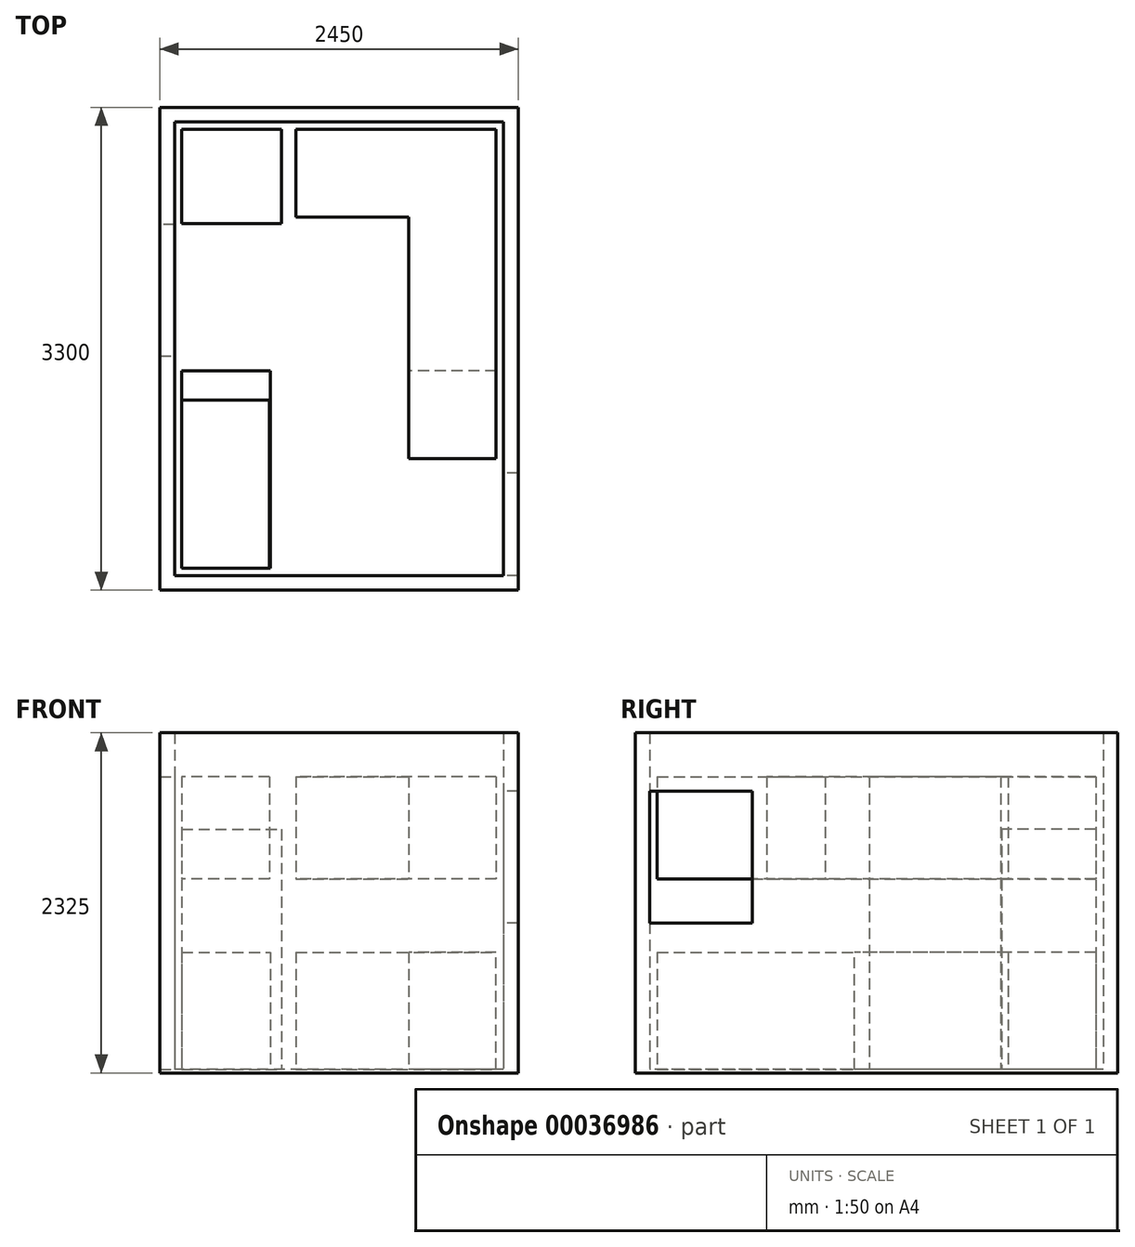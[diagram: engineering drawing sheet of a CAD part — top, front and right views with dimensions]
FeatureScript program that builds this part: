
annotation { "Feature Type Name" : "Feature", "Feature Type Description" : "" }
export const myFeature = defineFeature(function(context is Context, id is Id, definition is map)
    precondition{}
    {
        {
            var Q0;
            Q0=qCreatedBy(makeId("Top.planeOp"),FACE);
            var sketch = newSketch(context, id + "F0", { "sketchPlane" : qUnion([Q0])});
            skLineSegment(sketch, "E0.rect.bottom", {"start": v(1125, 1550) * mm, "end": v(-1125, 1550) * mm});
            skLineSegment(sketch, "E0.rect.top", {"start": v(1125, -1550) * mm, "end": v(-1125, -1550) * mm});
            skLineSegment(sketch, "E0.rect.left", {"start": v(1125, 1550) * mm, "end": v(1125, -1550) * mm});
            skLineSegment(sketch, "E0.rect.right", {"start": v(-1125, 1550) * mm, "end": v(-1125, -1550) * mm});
            skPoint(sketch, "E0.rect.middle", {"position": v(0, 0) * mm});
            skLineSegment(sketch, "E1.0", {"start": v(1225, 1650) * mm, "end": v(-1225, 1650) * mm});
            skLineSegment(sketch, "E1.1", {"start": v(1225, 1650) * mm, "end": v(1225, -1650) * mm});
            skLineSegment(sketch, "E1.2", {"start": v(1225, -1650) * mm, "end": v(-1225, -1650) * mm});
            skLineSegment(sketch, "E1.3", {"start": v(-1225, 1650) * mm, "end": v(-1225, -1650) * mm});
            skLineSegment(sketch, "E2", {"start": v(-1125, 850) * mm, "end": v(-1225, 850) * mm});
            skLineSegment(sketch, "E3", {"start": v(-1225, -50) * mm, "end": v(-1125, -50) * mm});
            skSolve(sketch);
        }
        {
            var Q0;
            {var subQ3=sQuery(id+"F0.wireOp",EDGE,"E0.rect.bottom");Q0=makeQuery(id+"F0.imprint","IMPRINT",FACE,{"disambiguationData":[TD([[makeQuery(id+"F0.imprint","IMPRINT",EDGE,{"derivedFrom":subQ3}),-1.0]])]});}
            extrude(context, id + "F1", {"entities" : qUnion([Q0]), "depth" : 2300 * mm});
        }
        {
            var Q0;
            Q0=makeQuery(id+"F1.opExtrude","SWEPT_FACE",FACE,{"disambiguationData":[OSD([sQuery(id+"F0.wireOp",EDGE,"E0.rect.left")])]});
            var sketch = newSketch(context, id + "F2", { "sketchPlane" : qUnion([Q0])});
            skLineSegment(sketch, "E4.bottom", {"start": v(1550, 1900) * mm, "end": v(850, 1900) * mm});
            skLineSegment(sketch, "E4.top", {"start": v(1550, 1000) * mm, "end": v(850, 1000) * mm});
            skLineSegment(sketch, "E4.left", {"start": v(1550, 1900) * mm, "end": v(1550, 1000) * mm});
            skLineSegment(sketch, "E4.right", {"start": v(850, 1900) * mm, "end": v(850, 1000) * mm});
            skSolve(sketch);
        }
        {
            var Q0;
            Q0 = qSketchRegion(id + "F2", true);
            extrude(context, id + "F3", {"entities" : qUnion([Q0]), "operationType" : NewBodyOperationType.REMOVE, "oppositeDirection" : true, "depth" : 512.68 * mm});
        }
        {
            var Q0;
            Q0=makeQuery(id+"F1.opExtrude","CAP_FACE",FACE,{"disambiguationData":[OSD([sQuery(id+"F0.wireOp",EDGE,"E0.rect.bottom"),sQuery(id+"F0.wireOp",EDGE,"E0.rect.top"),sQuery(id+"F0.wireOp",EDGE,"E0.rect.left"),sQuery(id+"F0.wireOp",EDGE,"E0.rect.right"),sQuery(id+"F0.wireOp",EDGE,"E1.0"),sQuery(id+"F0.wireOp",EDGE,"E1.1"),sQuery(id+"F0.wireOp",EDGE,"E1.2"),sQuery(id+"F0.wireOp",EDGE,"E1.3"),sQuery(id+"F0.wireOp",EDGE,"E2"),sQuery(id+"F0.wireOp",EDGE,"E3")])],"isStart":true});
            var sketch = newSketch(context, id + "F4", { "sketchPlane" : qUnion([Q0])});
            skLineSegment(sketch, "E5.bottom", {"start": v(-1225, -1650) * mm, "end": v(1225, -1650) * mm});
            skLineSegment(sketch, "E5.top", {"start": v(-1225, 1650) * mm, "end": v(1225, 1650) * mm});
            skLineSegment(sketch, "E5.left", {"start": v(-1225, -1650) * mm, "end": v(-1225, 1650) * mm});
            skLineSegment(sketch, "E5.right", {"start": v(1225, -1650) * mm, "end": v(1225, 1650) * mm});
            skSolve(sketch);
        }
        {
            var Q0;
            Q0 = qSketchRegion(id + "F4", true);
            extrude(context, id + "F5", {"entities" : qUnion([Q0]), "operationType" : NewBodyOperationType.ADD, "depth" : 25 * mm});
        }
        {
            var Q0;
            Q0=makeQuery(id+"F1.opExtrude","CAP_FACE",FACE,{"disambiguationData":[OSD([sQuery(id+"F0.wireOp",EDGE,"E0.rect.bottom"),sQuery(id+"F0.wireOp",EDGE,"E0.rect.top"),sQuery(id+"F0.wireOp",EDGE,"E0.rect.left"),sQuery(id+"F0.wireOp",EDGE,"E0.rect.right"),sQuery(id+"F0.wireOp",EDGE,"E1.0"),sQuery(id+"F0.wireOp",EDGE,"E1.1"),sQuery(id+"F0.wireOp",EDGE,"E1.2"),sQuery(id+"F0.wireOp",EDGE,"E1.3"),sQuery(id+"F0.wireOp",EDGE,"E2"),sQuery(id+"F0.wireOp",EDGE,"E3")])],"isStart":false});
            var sketch = newSketch(context, id + "F6", { "sketchPlane" : qUnion([Q0])});
            skLineSegment(sketch, "E6.bottom", {"start": v(-1125, 850) * mm, "end": v(-1225, 850) * mm});
            skLineSegment(sketch, "E6.top", {"start": v(-1125, -50) * mm, "end": v(-1225, -50) * mm});
            skLineSegment(sketch, "E6.left", {"start": v(-1125, 850) * mm, "end": v(-1125, -50) * mm});
            skLineSegment(sketch, "E6.right", {"start": v(-1225, 850) * mm, "end": v(-1225, -50) * mm});
            skSolve(sketch);
        }
        {
            var Q0;
            Q0 = qSketchRegion(id + "F6", true);
            extrude(context, id + "F7", {"entities" : qUnion([Q0]), "operationType" : NewBodyOperationType.ADD, "oppositeDirection" : true, "depth" : 300 * mm});
        }
        {
            var Q0;
            Q0=makeQuery(id+"F5.opExtrude","CAP_FACE",FACE,{"disambiguationData":[OSD([sQuery(id+"F4.wireOp",EDGE,"E5.bottom"),sQuery(id+"F4.wireOp",EDGE,"E5.top"),sQuery(id+"F4.wireOp",EDGE,"E5.left"),sQuery(id+"F4.wireOp",EDGE,"E5.right")])],"isStart":true});
            var sketch = newSketch(context, id + "F8", { "sketchPlane" : qUnion([Q0])});
            skLineSegment(sketch, "E7.bottom", {"start": v(-1075, 1500) * mm, "end": v(-395, 1500) * mm});
            skLineSegment(sketch, "E7.top", {"start": v(-1075, 855) * mm, "end": v(-395, 855) * mm});
            skLineSegment(sketch, "E7.left", {"start": v(-1075, 1500) * mm, "end": v(-1075, 855) * mm});
            skLineSegment(sketch, "E7.right", {"start": v(-395, 1500) * mm, "end": v(-395, 855) * mm});
            skSolve(sketch);
        }
        {
            var Q0;
            Q0 = qSketchRegion(id + "F8", true);
            extrude(context, id + "F9", {"entities" : qUnion([Q0]), "depth" : 1640 * mm});
        }
        {
            var Q0;
            Q0=makeQuery(id+"F5.opExtrude","CAP_FACE",FACE,{"disambiguationData":[OSD([sQuery(id+"F4.wireOp",EDGE,"E5.bottom"),sQuery(id+"F4.wireOp",EDGE,"E5.top"),sQuery(id+"F4.wireOp",EDGE,"E5.left"),sQuery(id+"F4.wireOp",EDGE,"E5.right")])],"isStart":true});
            var sketch = newSketch(context, id + "F10", { "sketchPlane" : qUnion([Q0])});
            skLineSegment(sketch, "E8.bottom", {"start": v(-295, 1500) * mm, "end": v(1075, 1500) * mm});
            skLineSegment(sketch, "E8.top", {"start": v(-295, 900) * mm, "end": v(1075, 900) * mm});
            skLineSegment(sketch, "E8.left", {"start": v(-295, 1500) * mm, "end": v(-295, 900) * mm});
            skLineSegment(sketch, "E8.right", {"start": v(1075, 1500) * mm, "end": v(1075, 900) * mm});
            skLineSegment(sketch, "E9.bottom", {"start": v(1075, 900) * mm, "end": v(475, 900) * mm});
            skLineSegment(sketch, "E9.top", {"start": v(1075, -1500) * mm, "end": v(475, -1500) * mm});
            skLineSegment(sketch, "E9.left", {"start": v(1075, 900) * mm, "end": v(1075, -1500) * mm});
            skLineSegment(sketch, "E9.right", {"start": v(475, 900) * mm, "end": v(475, -1500) * mm});
            skSolve(sketch);
        }
        {
            var Q0;
            Q0 = qSketchRegion(id + "F10", true);
            extrude(context, id + "F11", {"entities" : qUnion([Q0]), "depth" : 800 * mm});
        }
        {
            var Q0;
            Q0=makeQuery(id+"F11.opExtrude","CAP_FACE",FACE,{"disambiguationData":[OSD([sQuery(id+"F10.wireOp",EDGE,"E8.bottom"),sQuery(id+"F10.wireOp",EDGE,"E8.top"),sQuery(id+"F10.wireOp",EDGE,"E8.left"),sQuery(id+"F10.wireOp",EDGE,"E8.right")])],"isStart":false});
            cPlane(context, id + "F12", {"entities" : qUnion([Q0]), "cplaneType" : CPlaneType.OFFSET, "offset" : 500 * mm, "width" : 150 * mm, "height" : 150 * mm});
        }
        {
            var Q0;
            Q0=qCreatedBy(id+"F12.planeOp",FACE);
            var sketch = newSketch(context, id + "F13", { "sketchPlane" : qUnion([Q0])});
            skLineSegment(sketch, "E10.0.0", {"start": v(1075, 1500) * mm, "end": v(-295, 1500) * mm});
            skLineSegment(sketch, "E10.0.1", {"start": v(-295, 1500) * mm, "end": v(-295, 900) * mm});
            skLineSegment(sketch, "E10.0.2", {"start": v(-295, 900) * mm, "end": v(1075, 900) * mm});
            skLineSegment(sketch, "E10.0.3", {"start": v(1075, 900) * mm, "end": v(1075, 1500) * mm});
            skLineSegment(sketch, "E11.bottom", {"start": v(1075, 900) * mm, "end": v(475, 900) * mm});
            skLineSegment(sketch, "E11.top", {"start": v(1075, -750) * mm, "end": v(475, -750) * mm});
            skLineSegment(sketch, "E11.left", {"start": v(1075, 900) * mm, "end": v(1075, -750) * mm});
            skLineSegment(sketch, "E11.right", {"start": v(475, 900) * mm, "end": v(475, -750) * mm});
            skSolve(sketch);
        }
        {
            var Q0;
            Q0 = qSketchRegion(id + "F13", true);
            extrude(context, id + "F14", {"entities" : qUnion([Q0]), "depth" : 700 * mm});
        }
        {
            var Q0;
            Q0=makeQuery(id+"F5.opExtrude","CAP_FACE",FACE,{"disambiguationData":[OSD([sQuery(id+"F4.wireOp",EDGE,"E5.bottom"),sQuery(id+"F4.wireOp",EDGE,"E5.top"),sQuery(id+"F4.wireOp",EDGE,"E5.left"),sQuery(id+"F4.wireOp",EDGE,"E5.right")])],"isStart":true});
            var sketch = newSketch(context, id + "F15", { "sketchPlane" : qUnion([Q0])});
            skLineSegment(sketch, "E12.bottom", {"start": v(-1075, -350) * mm, "end": v(-475, -350) * mm});
            skLineSegment(sketch, "E12.top", {"start": v(-1075, -1500) * mm, "end": v(-475, -1500) * mm});
            skLineSegment(sketch, "E12.left", {"start": v(-1075, -350) * mm, "end": v(-1075, -1500) * mm});
            skLineSegment(sketch, "E12.right", {"start": v(-475, -350) * mm, "end": v(-475, -1500) * mm});
            skLineSegment(sketch, "E13.bottom", {"start": v(-1075, -1500) * mm, "end": v(-469.84, -1500) * mm});
            skLineSegment(sketch, "E13.top", {"start": v(-1075, -150) * mm, "end": v(-469.84, -150) * mm});
            skLineSegment(sketch, "E13.left", {"start": v(-1075, -1500) * mm, "end": v(-1075, -150) * mm});
            skLineSegment(sketch, "E13.right", {"start": v(-469.84, -1500) * mm, "end": v(-469.84, -150) * mm});
            skSolve(sketch);
        }
        {
            var Q0;
            Q0 = qSketchRegion(id + "F15", true);
            extrude(context, id + "F16", {"entities" : qUnion([Q0]), "depth" : 800 * mm});
        }
        {
            var Q0;
            Q0=qCreatedBy(id+"F12.planeOp",FACE);
            var sketch = newSketch(context, id + "F17", { "sketchPlane" : qUnion([Q0])});
            skLineSegment(sketch, "E14.0.0", {"start": v(-475, -350) * mm, "end": v(-1075, -350) * mm});
            skLineSegment(sketch, "E14.0.1", {"start": v(-1075, -350) * mm, "end": v(-1075, -1500) * mm});
            skLineSegment(sketch, "E14.0.2", {"start": v(-1075, -1500) * mm, "end": v(-475, -1500) * mm});
            skLineSegment(sketch, "E14.0.3", {"start": v(-475, -1500) * mm, "end": v(-475, -350) * mm});
            skSolve(sketch);
        }
        {
            var Q0;
            Q0 = qSketchRegion(id + "F17", true);
            extrude(context, id + "F18", {"entities" : qUnion([Q0]), "operationType" : NewBodyOperationType.ADD, "depth" : 700 * mm});
        }
        {
            var Q0;
            Q0=makeQuery(id+"F11.opExtrude","CAP_FACE",FACE,{"disambiguationData":[OSD([sQuery(id+"F10.wireOp",EDGE,"E8.bottom"),sQuery(id+"F10.wireOp",EDGE,"E8.top"),sQuery(id+"F10.wireOp",EDGE,"E8.left"),sQuery(id+"F10.wireOp",EDGE,"E8.right"),sQuery(id+"F10.wireOp",EDGE,"E9.top"),sQuery(id+"F10.wireOp",EDGE,"E9.left"),sQuery(id+"F10.wireOp",EDGE,"E9.right")])],"isStart":false});
            var sketch = newSketch(context, id + "F19", { "sketchPlane" : qUnion([Q0])});
            skLineSegment(sketch, "E15.bottom", {"start": v(1075, -1500) * mm, "end": v(475, -1500) * mm});
            skLineSegment(sketch, "E16.top", {"start": v(1075, -150) * mm, "end": v(475, -150) * mm});
            skLineSegment(sketch, "E16.left", {"start": v(1075, -1500) * mm, "end": v(1075, -150) * mm});
            skLineSegment(sketch, "E16.right", {"start": v(475, -1500) * mm, "end": v(475, -150) * mm});
            skSolve(sketch);
        }
        {
            var Q0;
            Q0 = qSketchRegion(id + "F19", true);
            extrude(context, id + "F20", {"entities" : qUnion([Q0]), "operationType" : NewBodyOperationType.REMOVE, "oppositeDirection" : true, "depth" : 800 * mm});
        }
    });
